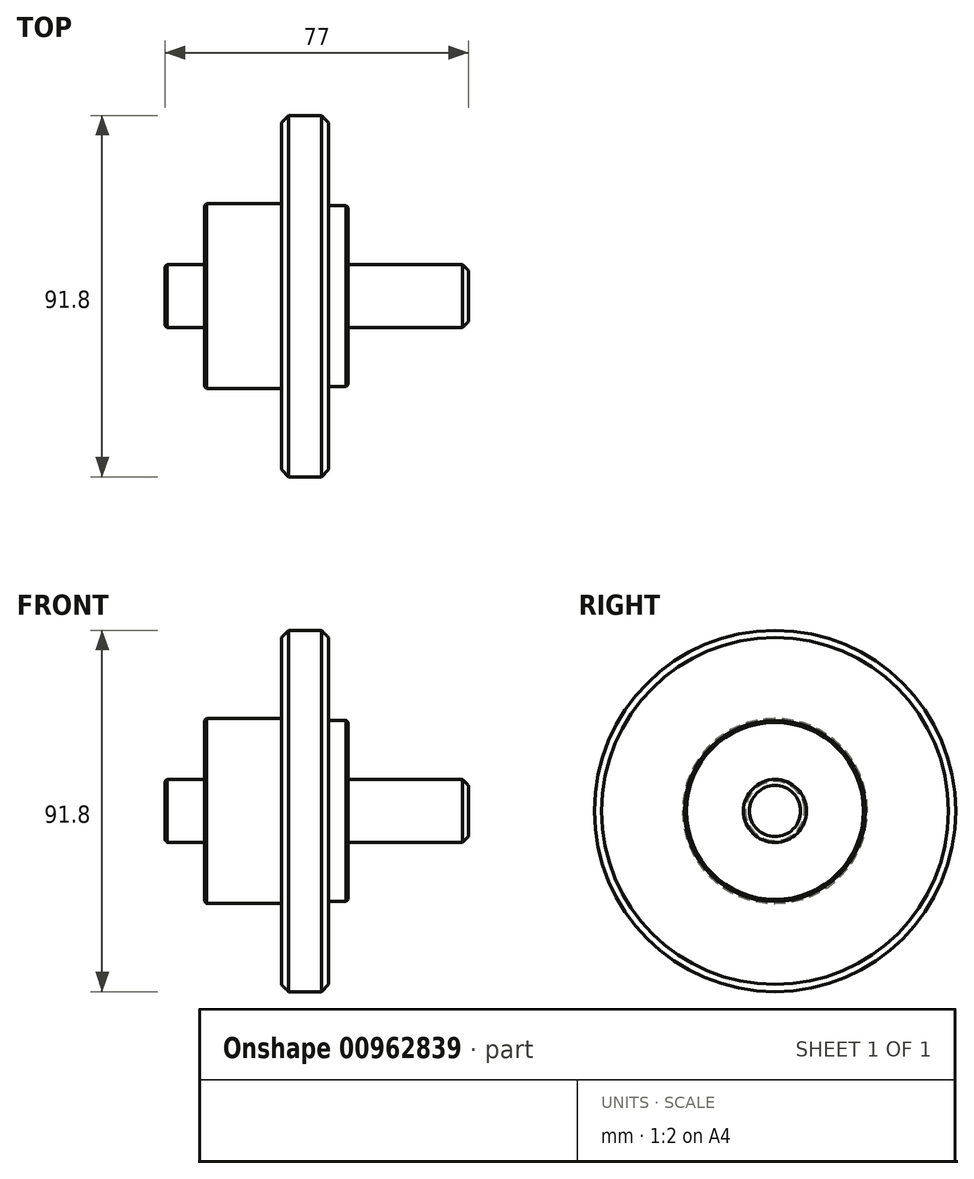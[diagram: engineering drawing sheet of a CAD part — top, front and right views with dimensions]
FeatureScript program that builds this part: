
annotation { "Feature Type Name" : "Feature", "Feature Type Description" : "" }
export const myFeature = defineFeature(function(context is Context, id is Id, definition is map)
    precondition{}
    {
        {
            var Q0;
            Q0=qCreatedBy(makeId("Front.planeOp"),FACE);
            var sketch = newSketch(context, id + "F0", { "sketchPlane" : qUnion([Q0])});
            skLineSegment(sketch, "E0", {"start": v(0, 0) * mm, "end": v(0, 8) * mm});
            skLineSegment(sketch, "E1", {"start": v(0, 8) * mm, "end": v(10, 8) * mm});
            skLineSegment(sketch, "E2", {"start": v(10, 8) * mm, "end": v(10, 23.5) * mm});
            skLineSegment(sketch, "E3", {"start": v(10, 23.5) * mm, "end": v(29.5, 23.5) * mm});
            skLineSegment(sketch, "E4", {"start": v(29.5, 23.5) * mm, "end": v(29.5, 45.9) * mm});
            skLineSegment(sketch, "E5", {"start": v(29.5, 45.9) * mm, "end": v(41.45, 45.9) * mm});
            skLineSegment(sketch, "E6", {"start": v(41.45, 45.9) * mm, "end": v(41.45, 23) * mm});
            skLineSegment(sketch, "E7", {"start": v(41.45, 23) * mm, "end": v(46.45, 23) * mm});
            skLineSegment(sketch, "E8", {"start": v(46.45, 23) * mm, "end": v(46.45, 8) * mm});
            skLineSegment(sketch, "E9", {"start": v(46.45, 8) * mm, "end": v(77, 8) * mm});
            skLineSegment(sketch, "E10", {"start": v(77, 8) * mm, "end": v(77, 0) * mm});
            skLineSegment(sketch, "E11", {"start": v(77, 0) * mm, "end": v(0, 0) * mm});
            skSolve(sketch);
        }
        {
            var Q0;
            Q0=makeQuery(id+"F0.imprint","IMPRINT",FACE,{"disambiguationData":[TD([[makeQuery(id+"F0.imprint","IMPRINT",EDGE,{"derivedFrom":sQuery(id+"F0.wireOp",EDGE,"E0")}),-1.0]])]});
            var Q1;
            Q1=sQuery(id+"F0.wireOp",EDGE,"E11");
            revolve(context, id + "F1", {"surfaceOperationType" : NewSurfaceOperationType.NEW, "entities" : qUnion([Q0]), "axis" : qUnion([Q1]), "revolveType" : RevolveType.FULL});
        }
        {
            var Q0;
            Q0=makeQuery(id+"F1.opRevolve","SWEPT_EDGE",EDGE,{"disambiguationData":[OSD([sQuery(id+"F0.wireOp",EDGE,"E0"),sQuery(id+"F0.wireOp",EDGE,"E1")])]});
            var Q1;
            Q1=makeQuery(id+"F1.opRevolve","SWEPT_EDGE",EDGE,{"disambiguationData":[OSD([sQuery(id+"F0.wireOp",EDGE,"E2"),sQuery(id+"F0.wireOp",EDGE,"E3")])]});
            var Q2;
            Q2=makeQuery(id+"F1.opRevolve","SWEPT_EDGE",EDGE,{"disambiguationData":[OSD([sQuery(id+"F0.wireOp",EDGE,"E7"),sQuery(id+"F0.wireOp",EDGE,"E8")])]});
            chamfer(context, id + "F2", {"entities" : qUnion([Q0, Q1, Q2]), "width" : 0.5 * mm, "tangentPropagation" : true});
        }
        {
            var Q0;
            Q0=makeQuery(id+"F1.opRevolve","SWEPT_EDGE",EDGE,{"disambiguationData":[OSD([sQuery(id+"F0.wireOp",EDGE,"E9"),sQuery(id+"F0.wireOp",EDGE,"E10")])]});
            chamfer(context, id + "F3", {"entities" : qUnion([Q0]), "width" : 1.5 * mm, "tangentPropagation" : true});
        }
        {
            var Q0;
            Q0=makeQuery(id+"F1.opRevolve","SWEPT_EDGE",EDGE,{"disambiguationData":[OSD([sQuery(id+"F0.wireOp",EDGE,"E5"),sQuery(id+"F0.wireOp",EDGE,"E6")])]});
            var Q1;
            Q1=makeQuery(id+"F1.opRevolve","SWEPT_EDGE",EDGE,{"disambiguationData":[OSD([sQuery(id+"F0.wireOp",EDGE,"E4"),sQuery(id+"F0.wireOp",EDGE,"E5")])]});
            chamfer(context, id + "F4", {"entities" : qUnion([Q0, Q1]), "width" : 1.82 * mm, "tangentPropagation" : true});
        }
    });
